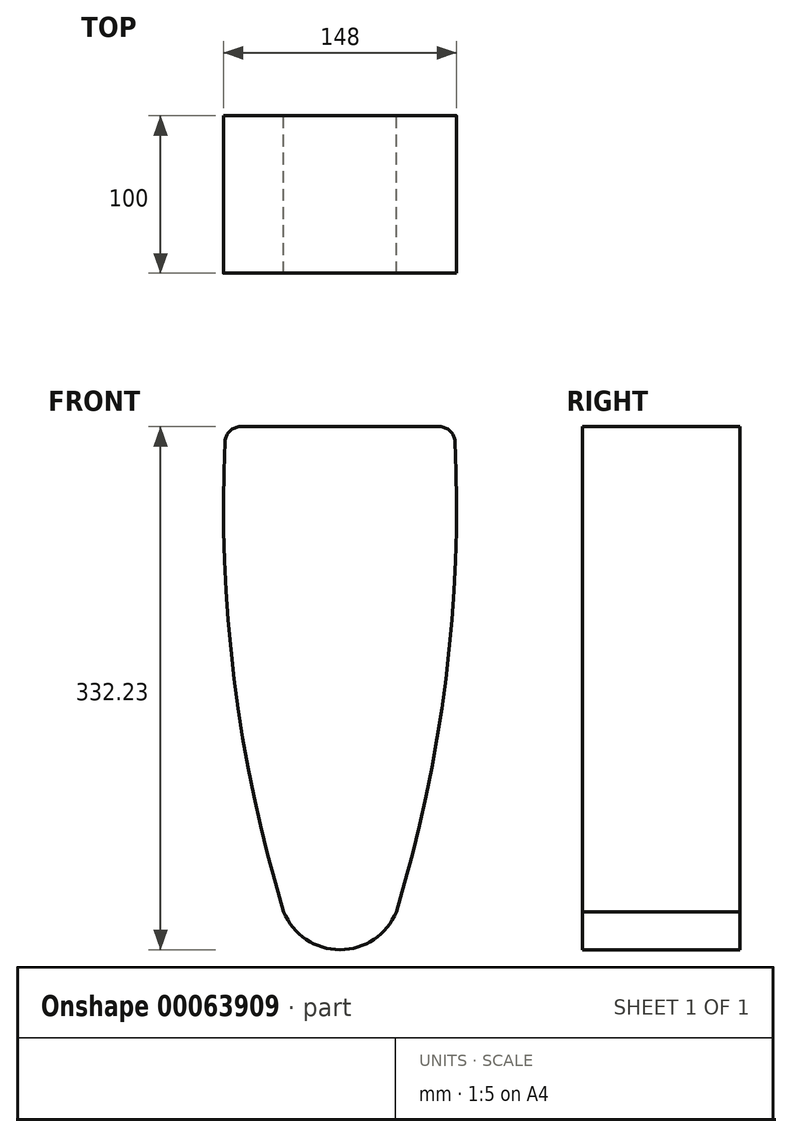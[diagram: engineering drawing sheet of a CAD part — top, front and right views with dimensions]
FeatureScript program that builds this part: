
annotation { "Feature Type Name" : "Feature", "Feature Type Description" : "" }
export const myFeature = defineFeature(function(context is Context, id is Id, definition is map)
    precondition{}
    {
        {
            var Q0;
            Q0=qCreatedBy(makeId("Front.planeOp"),FACE);
            var sketch = newSketch(context, id + "F0", { "sketchPlane" : qUnion([Q0])});
            skLineSegment(sketch, "E0", {"start": v(-59.43, 55.14) * mm, "end": v(66.6, 55.14) * mm});
            skArc(sketch, "E1", {"start": v(-69.42, 45.62) * mm, "mid": v(-63.63, -105.24) * mm, "end": v(-32.15, -252.9) * mm});
            skArc(sketch, "E2", {"start": v(39.32, -252.9) * mm, "mid": v(70.8, -105.24) * mm, "end": v(76.6, 45.62) * mm});
            skArc(sketch, "E3", {"start": v(-32.15, -252.9) * mm, "mid": v(3.59, -277.1) * mm, "end": v(39.32, -252.9) * mm});
            skPoint(sketch, "E4.visualSharp", {"position": v(-68.91, 55.14) * mm});
            skArc(sketch, "E4.filletArc", {"start": v(-59.43, 55.14) * mm, "mid": v(-66.33, 52.38) * mm, "end": v(-69.42, 45.62) * mm});
            skPoint(sketch, "E5.visualSharp", {"position": v(76.09, 55.14) * mm});
            skArc(sketch, "E5.filletArc", {"start": v(76.6, 45.62) * mm, "mid": v(73.5, 52.38) * mm, "end": v(66.6, 55.14) * mm});
            skSolve(sketch);
        }
        {
            var Q0;
            Q0=makeQuery(id+"F0.imprint","IMPRINT",FACE,{"disambiguationData":[TD([[makeQuery(id+"F0.imprint","IMPRINT",EDGE,{"derivedFrom":sQuery(id+"F0.wireOp",EDGE,"E0")}),-1.0]])]});
            extrude(context, id + "F1", {"entities" : qUnion([Q0]), "depth" : 100 * mm});
        }
    });
